# Revit family: TAG3
name_source: partatom
category: Furniture
units: mm (PartAtom-declared; Revit-internal decimal feet)

## family parameters
Always vertical = Yes
Cut with Voids When Loaded = No
OmniClass Number = 23.40.20.00
OmniClass Title = General Furniture and Specialties
Render Appearance Source = Family Geometry
Room Calculation Point = No
Shared = No
Work Plane-Based = No

## types (1)
- CCTYP10
    Default Elevation = 0 mm  [stored 0 ft]
    Description = 1 x Devens Black Side Chair Express, 1 x Auburn Black Conference Chair - Express, 1 x Single Monitor Arm, 1 x Bella 1050, Clamp Mount, 2 Outlet, USB A & C, White, 1 x TBL, REC, 2mm, 24Dx72Wx29H, HAL, GLD, 1 x Tbl, Rnd, 2mm, 36dx29h, Stlx36, Gld, 1 x Rectangular - 2mm Edge - 24D x 60W, 2 x Cbx 2d Full Depth Lat 24dx28hx30w, 1 x CBX Wall Mounted L Shelf Vertical 45Hx60Wx12D, 1 x Cbx Single Door Tower Hinge Left 24dx74hx12w, 2 x Cbx Tackboard Wall Mount 45hx36w
    Exported From CET Designer = Yes
    Manufacturer = AIS
    Model = 4657
    Show CCTYP10 = Yes
    VisibilityIndex = 0

note: [stored X ft] marks values corroborated as IEEE doubles in the binary element streams (Revit-internal decimal feet)

## geometry (parser evidence)
native form markers: Sweep x3
no freeform markers — native parametric forms only
